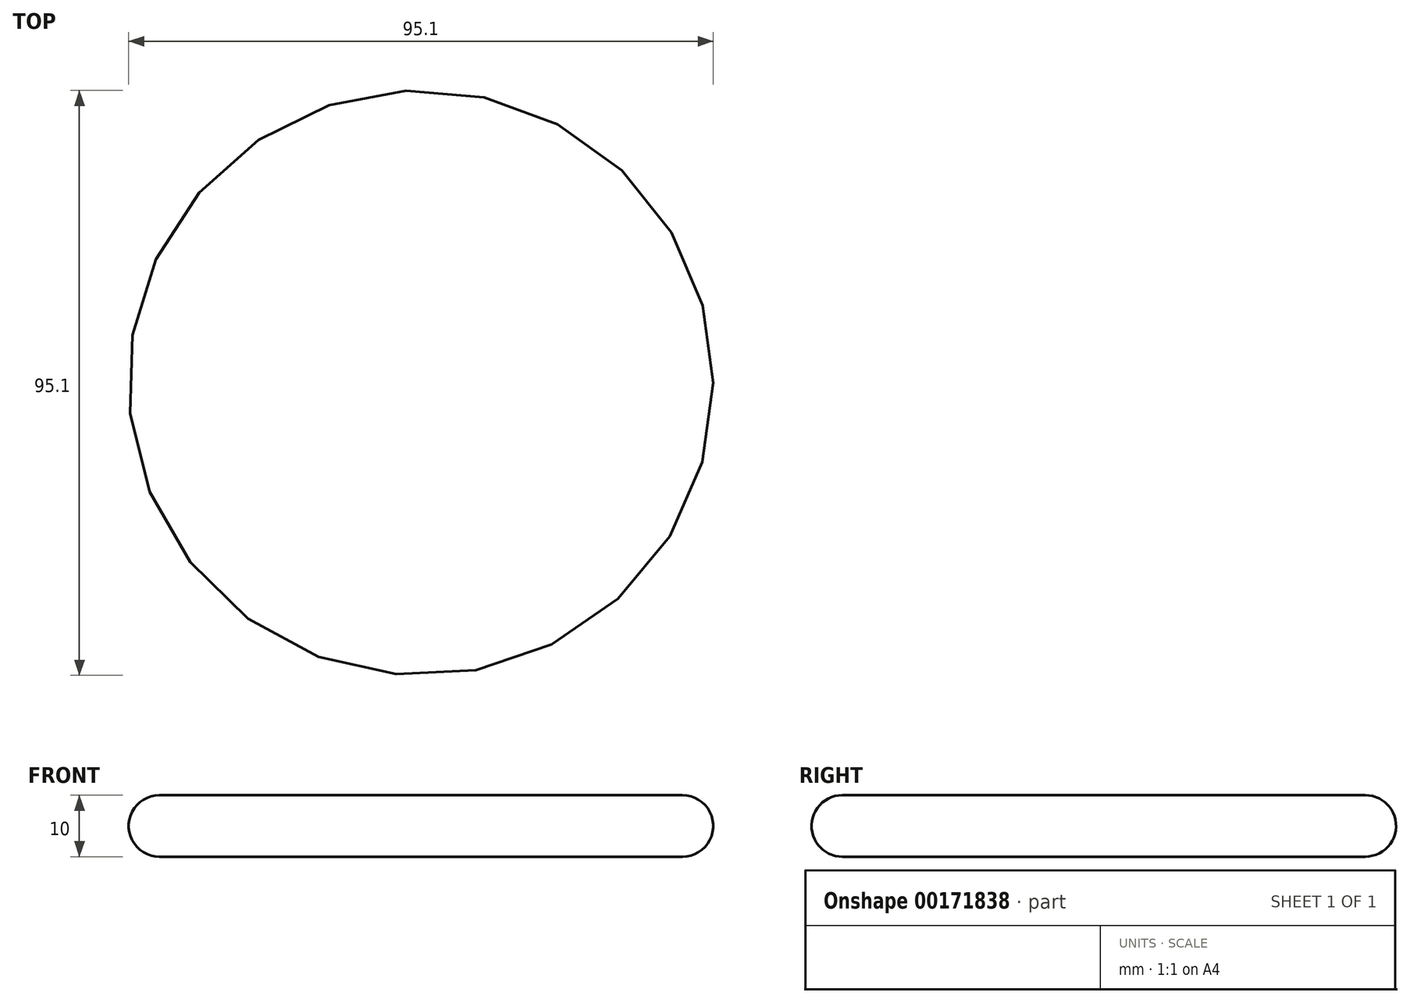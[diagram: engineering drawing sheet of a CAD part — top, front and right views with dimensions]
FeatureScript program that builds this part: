
annotation { "Feature Type Name" : "Feature", "Feature Type Description" : "" }
export const myFeature = defineFeature(function(context is Context, id is Id, definition is map)
    precondition{}
    {
        {
            var Q0;
            Q0=qCreatedBy(makeId("Top.planeOp"),FACE);
            var sketch = newSketch(context, id + "F0", { "sketchPlane" : qUnion([Q0])});
            skCircle(sketch, "E0", {"center": v(0, 0) * mm, "radius": 47.55 * mm});
            skSolve(sketch);
        }
        {
            var Q0;
            Q0 = qSketchRegion(id + "F0", true);
            extrude(context, id + "F1", {"entities" : qUnion([Q0]), "depth" : 10 * mm});
        }
        {
            var Q0;
            Q0=makeQuery(id+"F1.opExtrude","CAP_EDGE",EDGE,{"disambiguationData":[OSD([sQuery(id+"F0.wireOp",EDGE,"E0")])],"isStart":false});
            fillet(context, id + "F2", {"entities" : qUnion([Q0]), "radius" : 5 * mm, "tangentPropagation" : true, "allowEdgeOverflow" : false});
        }
        {
            var Q0;
            Q0=makeQuery(id+"F1.opExtrude","CAP_EDGE",EDGE,{"disambiguationData":[OSD([sQuery(id+"F0.wireOp",EDGE,"E0")])],"isStart":true});
            fillet(context, id + "F3", {"entities" : qUnion([Q0]), "radius" : 5 * mm, "tangentPropagation" : true, "allowEdgeOverflow" : false});
        }
    });
